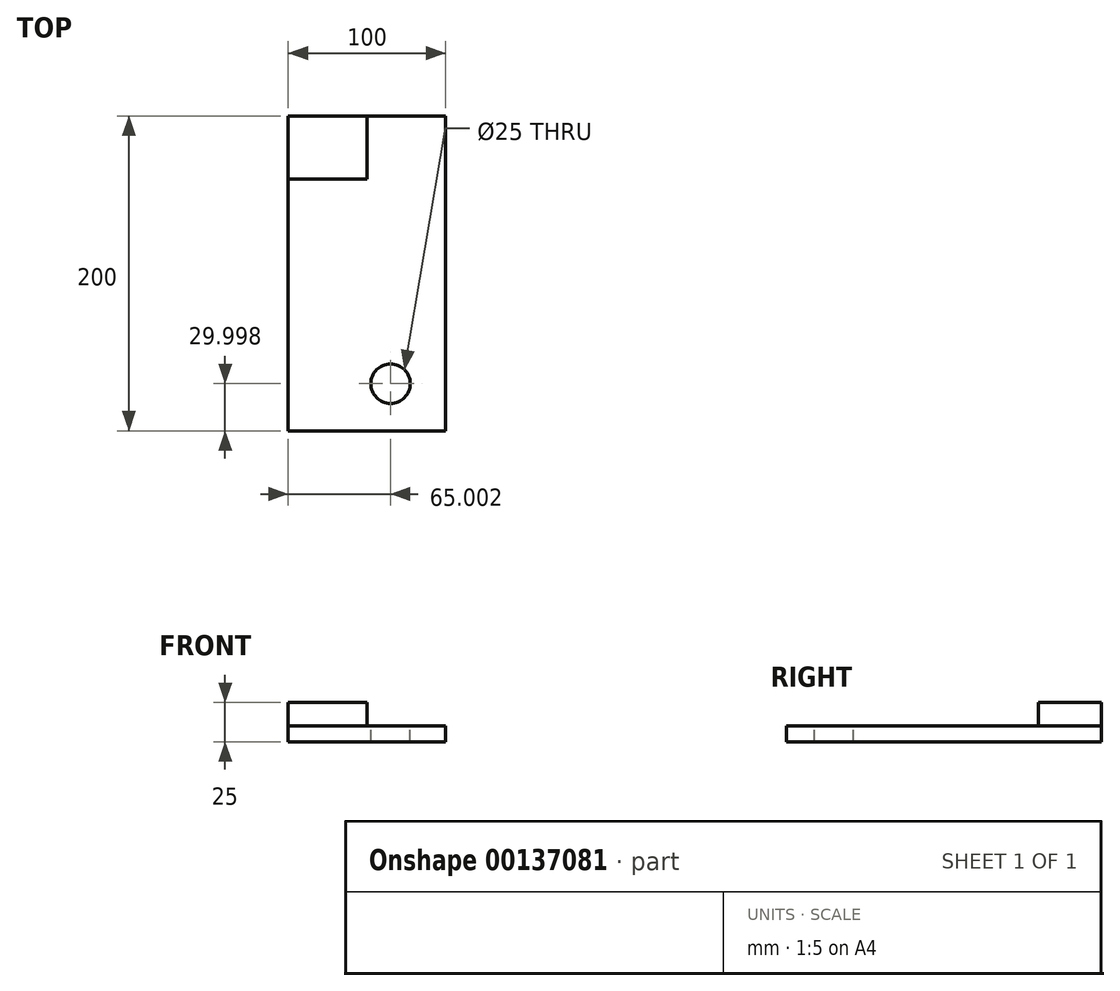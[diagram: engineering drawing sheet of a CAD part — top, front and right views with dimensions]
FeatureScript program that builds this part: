
annotation { "Feature Type Name" : "Feature", "Feature Type Description" : "" }
export const myFeature = defineFeature(function(context is Context, id is Id, definition is map)
    precondition{}
    {
        {
            var Q0;
            Q0=qCreatedBy(makeId("Top.planeOp"),FACE);
            var sketch = newSketch(context, id + "F0", { "sketchPlane" : qUnion([Q0])});
            skLineSegment(sketch, "E0.bottom", {"start": v(-67.35, 105.15) * mm, "end": v(32.65, 105.15) * mm});
            skLineSegment(sketch, "E0.top", {"start": v(-67.35, -94.85) * mm, "end": v(32.65, -94.85) * mm});
            skLineSegment(sketch, "E0.left", {"start": v(-67.35, 105.15) * mm, "end": v(-67.35, -94.85) * mm});
            skLineSegment(sketch, "E0.right", {"start": v(32.65, 105.15) * mm, "end": v(32.65, -94.85) * mm});
            skSolve(sketch);
        }
        {
            var Q0;
            Q0 = qSketchRegion(id + "F0", true);
            extrude(context, id + "F1", {"entities" : qUnion([Q0]), "depth" : 10 * mm});
        }
        {
            var Q0;
            Q0=qCreatedBy(makeId("Top.planeOp"),FACE);
            var sketch = newSketch(context, id + "F2", { "sketchPlane" : qUnion([Q0])});
            skLineSegment(sketch, "E1.bottom", {"start": v(-67.35, 105.15) * mm, "end": v(-17.35, 105.15) * mm});
            skLineSegment(sketch, "E1.top", {"start": v(-67.35, 65.15) * mm, "end": v(-17.35, 65.15) * mm});
            skLineSegment(sketch, "E1.left", {"start": v(-67.35, 105.15) * mm, "end": v(-67.35, 65.15) * mm});
            skLineSegment(sketch, "E1.right", {"start": v(-17.35, 105.15) * mm, "end": v(-17.35, 65.15) * mm});
            skSolve(sketch);
        }
        {
            var Q0;
            Q0=makeQuery(id+"F2.imprint","IMPRINT",FACE,{"disambiguationData":[TD([[makeQuery(id+"F2.imprint","IMPRINT",EDGE,{"derivedFrom":sQuery(id+"F2.wireOp",EDGE,"E1.bottom")}),-1.0]])]});
            extrude(context, id + "F3", {"entities" : qUnion([Q0]), "operationType" : NewBodyOperationType.ADD, "depth" : 25 * mm});
        }
        {
            var Q0;
            Q0=makeQuery(id+"F1.opExtrude","CAP_FACE",FACE,{"disambiguationData":[OSD([sQuery(id+"F0.wireOp",EDGE,"E0.bottom"),sQuery(id+"F0.wireOp",EDGE,"E0.top"),sQuery(id+"F0.wireOp",EDGE,"E0.left"),sQuery(id+"F0.wireOp",EDGE,"E0.right")])],"isStart":false});
            var sketch = newSketch(context, id + "F4", { "sketchPlane" : qUnion([Q0])});
            skCircle(sketch, "E2", {"center": v(-2.35, -64.85) * mm, "radius": 12.5 * mm});
            skSolve(sketch);
        }
        {
            var Q0;
            Q0=makeQuery(id+"F4.imprint","IMPRINT",FACE,{"disambiguationData":[TD([[makeQuery(id+"F4.imprint","IMPRINT",EDGE,{"derivedFrom":sQuery(id+"F4.wireOp",EDGE,"E2")}),1.0]])]});
            extrude(context, id + "F5", {"entities" : qUnion([Q0]), "operationType" : NewBodyOperationType.REMOVE, "endBound" : BoundingType.THROUGH_ALL, "oppositeDirection" : true, "depth" : 25.4 * mm});
        }
    });
